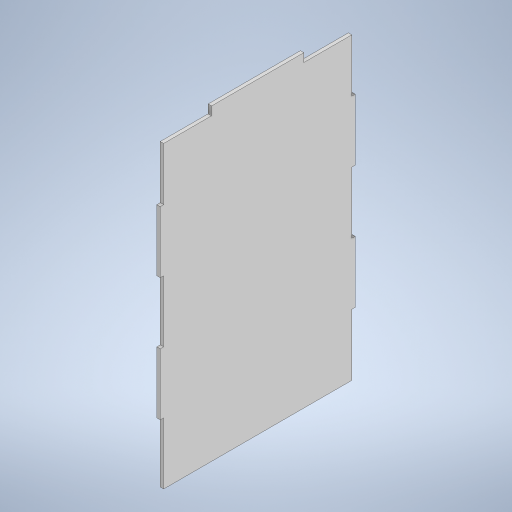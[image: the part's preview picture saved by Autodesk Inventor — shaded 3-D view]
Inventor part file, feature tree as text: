
AUTODESK INVENTOR PART (.ipt)
format: ipt  version: 2023 (Build 270158000, 158)  size: 254,976 bytes
history: native  units: mm
features: extrude x3, sketch x3
ambient origin geometry x8: Origin, YZ Plane, XZ Plane, XY Plane, X Axis, Y Axis, Z Axis, Center Point
bodies: Solid1 (feature_tree)
feature tree (6):
  extrude  "Extrusion1"  Depth=180.0mm
  extrude  "Extrusion2"  Depth=30.0mm
  extrude  "Extrusion3"  Depth=5.0mm
  sketch  "Sketch1"  dims[d0=114.0mm d1=180.0mm]
  sketch  "Sketch2"  dims[d2=2.0mm d3=0.0mm d4=30.0mm]
  sketch  "Sketch3"  dims[d5=30.0mm d6=5.0mm d7=2.0mm d8=0.0mm d9=2.0mm d10=2.0mm d11=36.0mm d12=36.0mm d13=36.0mm d14=36.0mm d15=36.0mm d16=2.0mm d17=0.0mm]
